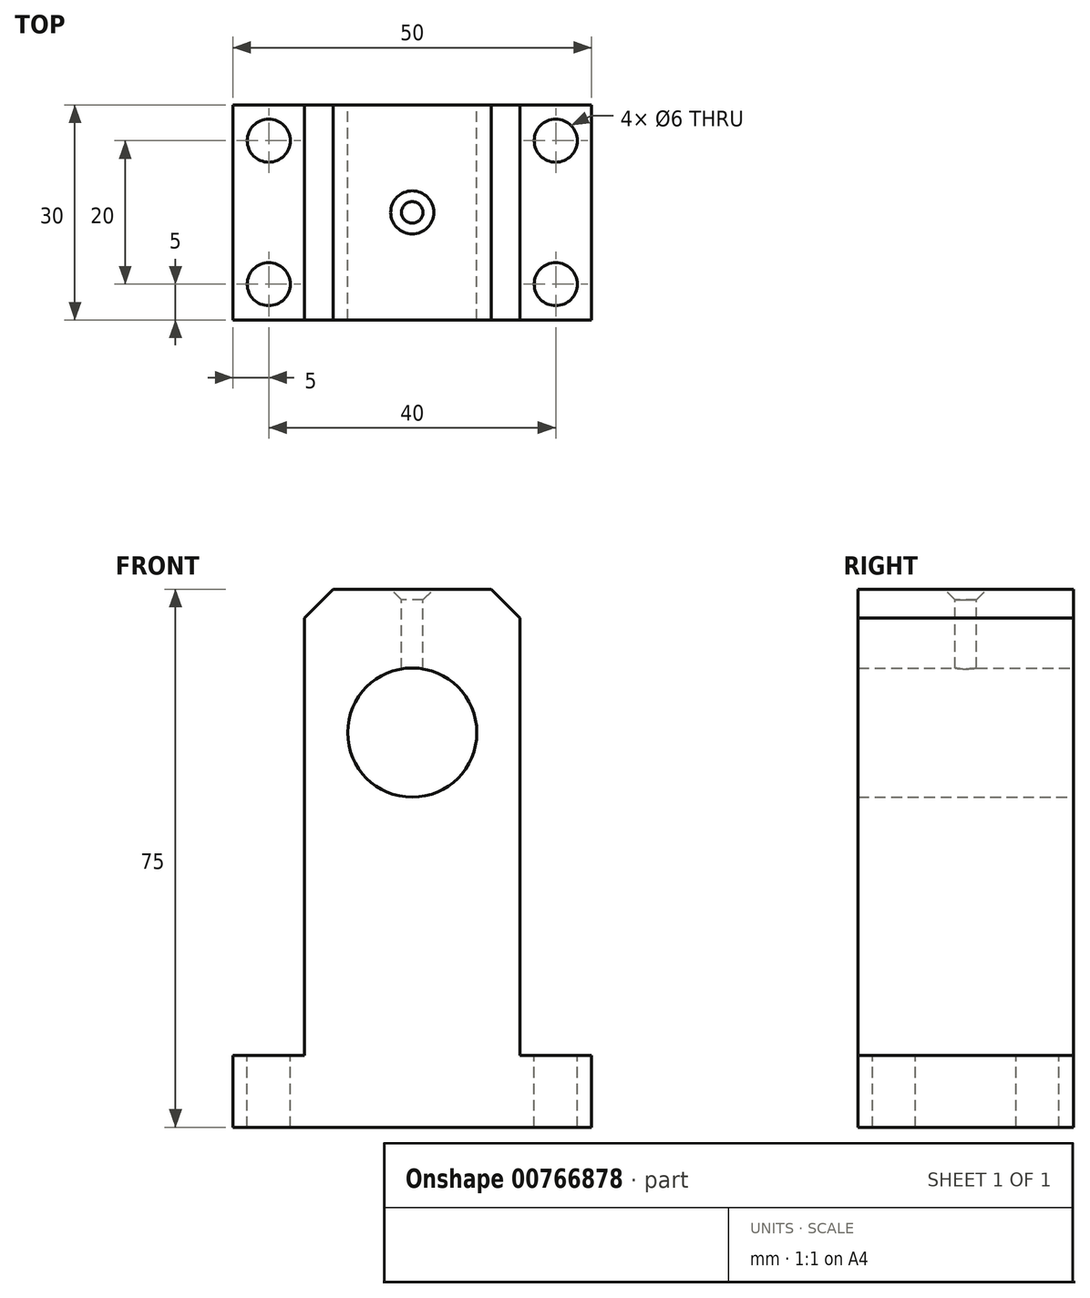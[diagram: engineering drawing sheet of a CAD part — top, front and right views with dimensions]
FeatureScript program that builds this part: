
annotation { "Feature Type Name" : "Feature", "Feature Type Description" : "" }
export const myFeature = defineFeature(function(context is Context, id is Id, definition is map)
    precondition{}
    {
        {
            var Q0;
            Q0=qCreatedBy(makeId("Front.planeOp"),FACE);
            var sketch = newSketch(context, id + "F0", { "sketchPlane" : qUnion([Q0])});
            skLineSegment(sketch, "E0", {"start": v(0, 0) * mm, "end": v(50, 0) * mm});
            skLineSegment(sketch, "E1", {"start": v(50, 0) * mm, "end": v(50, 10) * mm});
            skLineSegment(sketch, "E2", {"start": v(50, 10) * mm, "end": v(40, 10) * mm});
            skLineSegment(sketch, "E3", {"start": v(40, 10) * mm, "end": v(40, 75) * mm});
            skLineSegment(sketch, "E4", {"start": v(40, 75) * mm, "end": v(10, 75) * mm});
            skLineSegment(sketch, "E5", {"start": v(10, 75) * mm, "end": v(10, 10) * mm});
            skLineSegment(sketch, "E6", {"start": v(10, 10) * mm, "end": v(0, 10) * mm});
            skLineSegment(sketch, "E7", {"start": v(0, 10) * mm, "end": v(0, 0) * mm});
            skCircle(sketch, "E8", {"center": v(25, 55) * mm, "radius": 9 * mm});
            skSolve(sketch);
        }
        {
            var Q0;
            Q0=makeQuery(id+"F0.imprint","IMPRINT",FACE,{"disambiguationData":[TD([[makeQuery(id+"F0.imprint","IMPRINT",EDGE,{"derivedFrom":sQuery(id+"F0.wireOp",EDGE,"E0")}),1.0]])]});
            extrude(context, id + "F1", {"entities" : qUnion([Q0]), "depth" : 15 * mm, "offsetDistance" : 25 * mm, "hasSecondDirection" : true, "secondDirectionOppositeDirection" : true, "secondDirectionDepth" : 15 * mm});
        }
        {
            var Q0;
            Q0=makeQuery(id+"F1.opExtrude","SWEPT_FACE",FACE,{"disambiguationData":[OSD([sQuery(id+"F0.wireOp",EDGE,"E4")])]});
            var sketch = newSketch(context, id + "F2", { "sketchPlane" : qUnion([Q0])});
            skPoint(sketch, "E9", {"position": v(25, 0) * mm});
            skSolve(sketch);
        }
        {
            var Q0;
            Q0=sQuery(id+"F2.wireOp",VERTEX,"E9");
            var Q1;
            Q1=makeQuery(id+"F1.opExtrude","SWEPT_BODY",BODY,{"disambiguationData":[OSD([sQuery(id+"F0.wireOp",EDGE,"E0"),sQuery(id+"F0.wireOp",EDGE,"E1"),sQuery(id+"F0.wireOp",EDGE,"E2"),sQuery(id+"F0.wireOp",EDGE,"E3"),sQuery(id+"F0.wireOp",EDGE,"E4"),sQuery(id+"F0.wireOp",EDGE,"E5"),sQuery(id+"F0.wireOp",EDGE,"E6"),sQuery(id+"F0.wireOp",EDGE,"E7"),sQuery(id+"F0.wireOp",EDGE,"E8")])]});
            hole(context, id + "F3", {"style" : HoleStyle.C_SINK, "endStyle" : HoleEndStyle.BLIND, "holeDiameter" : 3 * mm, "cSinkDiameter" : 6 * mm, "cSinkAngle" : 90 * degree, "majorDiameter" : 5 * mm, "holeDepth" : 20 * mm, "isTappedThrough" : true, "tappedDepth" : 12 * mm, "tapClearance" : 3, "locations" : qUnion([Q0]), "scope" : qUnion([Q1])});
        }
        {
            var Q0;
            Q0=makeQuery(id+"F1.opExtrude","SWEPT_FACE",FACE,{"disambiguationData":[OSD([sQuery(id+"F0.wireOp",EDGE,"E6")])]});
            var sketch = newSketch(context, id + "F4", { "sketchPlane" : qUnion([Q0])});
            skCircle(sketch, "E10", {"center": v(5, 10) * mm, "radius": 3 * mm});
            skCircle(sketch, "E11", {"center": v(5, -10) * mm, "radius": 3 * mm});
            skCircle(sketch, "E12", {"center": v(45, -10) * mm, "radius": 3 * mm});
            skCircle(sketch, "E13", {"center": v(45, 10) * mm, "radius": 3 * mm});
            skSolve(sketch);
        }
        {
            var Q0;
            Q0=makeQuery(id+"F4.imprint","IMPRINT",FACE,{"disambiguationData":[TD([[makeQuery(id+"F4.imprint","IMPRINT",EDGE,{"derivedFrom":sQuery(id+"F4.wireOp",EDGE,"E10")}),1.0]])]});
            var Q1;
            Q1=makeQuery(id+"F4.imprint","IMPRINT",FACE,{"disambiguationData":[TD([[makeQuery(id+"F4.imprint","IMPRINT",EDGE,{"derivedFrom":sQuery(id+"F4.wireOp",EDGE,"E11")}),1.0]])]});
            var Q2;
            Q2=makeQuery(id+"F4.imprint","IMPRINT",FACE,{"disambiguationData":[TD([[makeQuery(id+"F4.imprint","IMPRINT",EDGE,{"derivedFrom":sQuery(id+"F4.wireOp",EDGE,"E12")}),1.0]])]});
            var Q3;
            Q3=makeQuery(id+"F4.imprint","IMPRINT",FACE,{"disambiguationData":[TD([[makeQuery(id+"F4.imprint","IMPRINT",EDGE,{"derivedFrom":sQuery(id+"F4.wireOp",EDGE,"E13")}),1.0]])]});
            extrude(context, id + "F5", {"entities" : qUnion([Q0, Q1, Q2, Q3]), "operationType" : NewBodyOperationType.REMOVE, "oppositeDirection" : true, "depth" : 10 * mm, "offsetDistance" : 25 * mm});
        }
        {
            var Q0;
            Q0=makeQuery(id+"F1.opExtrude","SWEPT_EDGE",EDGE,{"disambiguationData":[OSD([sQuery(id+"F0.wireOp",EDGE,"E3"),sQuery(id+"F0.wireOp",EDGE,"E4")])]});
            var Q1;
            Q1=makeQuery(id+"F1.opExtrude","SWEPT_EDGE",EDGE,{"disambiguationData":[OSD([sQuery(id+"F0.wireOp",EDGE,"E4"),sQuery(id+"F0.wireOp",EDGE,"E5")])]});
            chamfer(context, id + "F6", {"entities" : qUnion([Q0, Q1]), "width" : 4 * mm, "tangentPropagation" : true});
        }
    });
